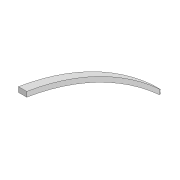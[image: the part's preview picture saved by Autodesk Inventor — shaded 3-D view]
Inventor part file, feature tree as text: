
AUTODESK INVENTOR PART (.ipt)
format: ipt  version: 2022 (Build 260153000, 153)  size: 125,952 bytes
history: native  units: mm
features: extrude x3, sketch x3, projected_geometry x2, fillet x1
ambient origin geometry x8: Origin, YZ Plane, XZ Plane, XY Plane, X Axis, Y Axis, Z Axis, Center Point
bodies: Solid1 (feature_tree)
feature tree (9):
  extrude  "Extrusion1"  Depth=10.0mm
  extrude  "Extrusion2"  Depth=30.0mm
  fillet  "Fillet1"  Radius=120.0mm
  extrude  "Extrusion3"  Depth=2.0mm TaperAngle=0.0deg
  sketch  "Sketch1"  dims[d0=160.0mm d1=10.0mm]
  sketch  "Sketch2"  dims[d2=3.3mm d3=30.0mm d5=120.0mm]
  projected_geometry  "Projected Loop1"
  projected_geometry  "Projected Loop2"
  sketch  "Sketch3"  dims[d6=3.3mm d7=6.0mm d8=0.0mm d9=6.0mm d10=373.775mm d11=90.0mm d12=10.0mm d13=0.0mm d14=2.0mm d15=100.0mm d16=0.0mm]
